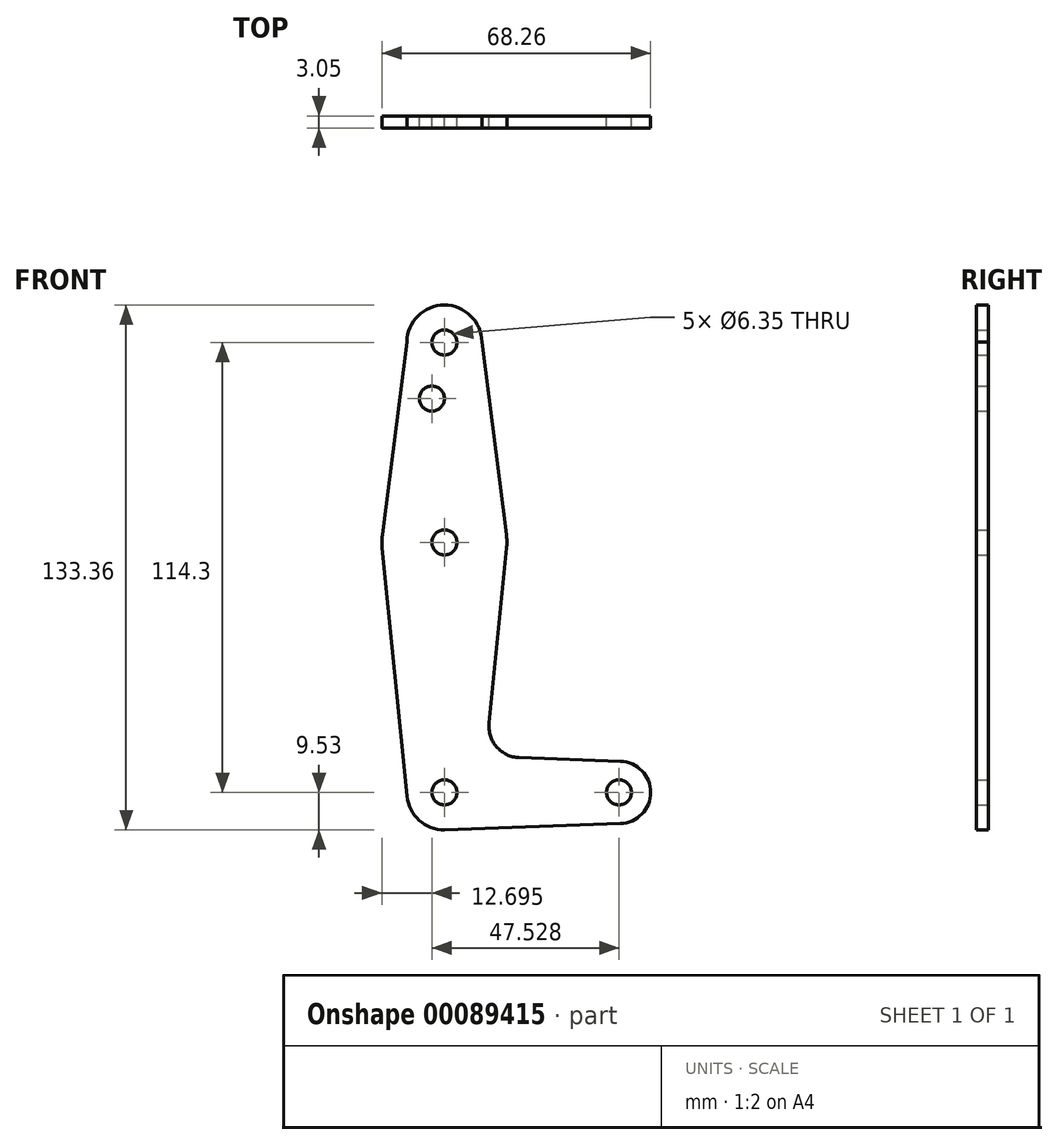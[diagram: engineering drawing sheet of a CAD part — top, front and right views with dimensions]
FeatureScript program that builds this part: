
annotation { "Feature Type Name" : "Feature", "Feature Type Description" : "" }
export const myFeature = defineFeature(function(context is Context, id is Id, definition is map)
    precondition{}
    {
        {
            var Q0;
            Q0=qCreatedBy(makeId("Front.planeOp"),FACE);
            var sketch = newSketch(context, id + "F0", { "sketchPlane" : qUnion([Q0])});
            skLineSegment(sketch, "E0", {"start": v(0, 114.3) * mm, "end": v(0, 0) * mm, "construction": true});
            skLineSegment(sketch, "E1", {"start": v(0, 0) * mm, "end": v(44.45, 0) * mm, "construction": true});
            skCircle(sketch, "E2", {"center": v(0, 114.3) * mm, "radius": 9.53 * mm});
            skCircle(sketch, "E3", {"center": v(0, 0) * mm, "radius": 9.53 * mm});
            skCircle(sketch, "E4", {"center": v(44.45, 0) * mm, "radius": 7.94 * mm});
            skCircle(sketch, "E5", {"center": v(0, 63.5) * mm, "radius": 15.88 * mm});
            skLineSegment(sketch, "E6", {"start": v(0, -9.53) * mm, "end": v(44.73, -7.93) * mm});
            skLineSegment(sketch, "E7", {"start": v(-9.52, 114.44) * mm, "end": v(-15.75, 65.5) * mm});
            skLineSegment(sketch, "E8", {"start": v(9.52, 114.44) * mm, "end": v(15.75, 65.5) * mm});
            skCircle(sketch, "E9", {"center": v(0, 0) * mm, "radius": 3.18 * mm});
            skCircle(sketch, "E10", {"center": v(44.35, 0.01) * mm, "radius": 3.18 * mm});
            skCircle(sketch, "E11", {"center": v(0.02, 63.52) * mm, "radius": 3.18 * mm});
            skCircle(sketch, "E12", {"center": v(0, 114.3) * mm, "radius": 3.18 * mm});
            skCircle(sketch, "E13", {"center": v(-3.17, 100.05) * mm, "radius": 3.18 * mm});
            skLineSegment(sketch, "E14", {"start": v(-15.81, 62.07) * mm, "end": v(-9.48, -0.95) * mm});
            skLineSegment(sketch, "E15", {"start": v(15.81, 62.07) * mm, "end": v(11.34, 17.59) * mm});
            skLineSegment(sketch, "E16", {"start": v(18.97, 8.85) * mm, "end": v(44.73, 7.93) * mm});
            skPoint(sketch, "E17.newPointB", {"position": v(0, 9.53) * mm});
            skArc(sketch, "E17.filletArc", {"start": v(11.34, 17.59) * mm, "mid": v(13.26, 11.57) * mm, "end": v(18.97, 8.85) * mm});
            skSolve(sketch);
        }
        {
            var Q0;
            Q0=makeQuery(id+"F0.imprint","IMPRINT",FACE,{"disambiguationData":[TD([[makeQuery(id+"F0.imprint","IMPRINT",EDGE,{"derivedFrom":sQuery(id+"F0.wireOp",EDGE,"E12")}),-1.0]])]});
            var Q1;
            {var subQ0=sQuery(id+"F0.wireOp",EDGE,"E7");Q1=makeQuery(id+"F0.imprint","IMPRINT",FACE,{"disambiguationData":[TD([[makeQuery(id+"F0.imprint","IMPRINT",EDGE,{"derivedFrom":subQ0}),1.0]])]});}
            var Q2;
            Q2=makeQuery(id+"F0.imprint","IMPRINT",FACE,{"disambiguationData":[TD([[makeQuery(id+"F0.imprint","IMPRINT",EDGE,{"derivedFrom":sQuery(id+"F0.wireOp",EDGE,"E11")}),-1.0]])]});
            var Q3;
            {var subQ11=sQuery(id+"F0.wireOp",EDGE,"E16");Q3=makeQuery(id+"F0.imprint","IMPRINT",FACE,{"disambiguationData":[TD([[makeQuery(id+"F0.imprint","IMPRINT",EDGE,{"derivedFrom":subQ11}),-1.0]])]});}
            var Q4;
            Q4=makeQuery(id+"F0.imprint","IMPRINT",FACE,{"disambiguationData":[TD([[makeQuery(id+"F0.imprint","IMPRINT",EDGE,{"derivedFrom":sQuery(id+"F0.wireOp",EDGE,"E9")}),-1.0]])]});
            var Q5;
            Q5=makeQuery(id+"F0.imprint","IMPRINT",FACE,{"disambiguationData":[TD([[makeQuery(id+"F0.imprint","IMPRINT",EDGE,{"derivedFrom":sQuery(id+"F0.wireOp",EDGE,"E10")}),-1.0]])]});
            extrude(context, id + "F1", {"entities" : qUnion([Q0, Q1, Q2, Q3, Q4, Q5]), "depth" : 3.05 * mm});
        }
    });
